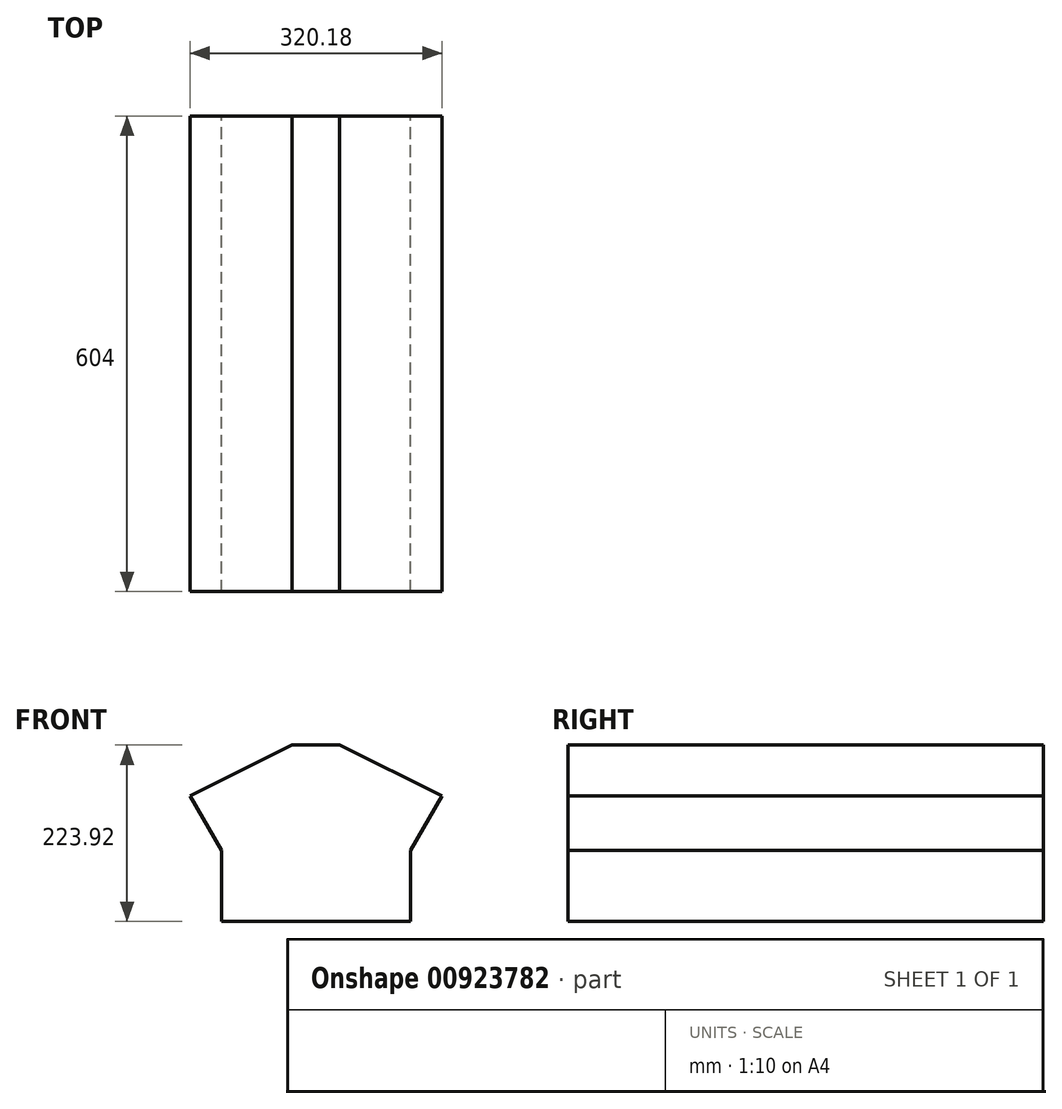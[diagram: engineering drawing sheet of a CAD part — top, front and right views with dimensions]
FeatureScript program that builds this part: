
annotation { "Feature Type Name" : "Feature", "Feature Type Description" : "" }
export const myFeature = defineFeature(function(context is Context, id is Id, definition is map)
    precondition{}
    {
        {
            var Q0;
            Q0=qCreatedBy(makeId("Front.planeOp"),FACE);
            var sketch = newSketch(context, id + "F0", { "sketchPlane" : qUnion([Q0])});
            skLineSegment(sketch, "E0", {"start": v(0, 0) * mm, "end": v(120, 0) * mm});
            skLineSegment(sketch, "E1", {"start": v(120, 0) * mm, "end": v(120, 90) * mm});
            skLineSegment(sketch, "E2", {"start": v(120, 90) * mm, "end": v(160.1, 159.44) * mm});
            skLineSegment(sketch, "E3", {"start": v(160.1, 159.44) * mm, "end": v(30.22, 223.92) * mm});
            skLineSegment(sketch, "E4", {"start": v(30.22, 223.92) * mm, "end": v(0, 223.92) * mm});
            skLineSegment(sketch, "E5", {"start": v(0, 223.92) * mm, "end": v(0, 0) * mm, "construction": true});
            skPoint(sketch, "E6.startSnap0", {"position": v(95.15, 191.68) * mm});
            skLineSegment(sketch, "E7", {"start": v(95.15, 191.68) * mm, "end": v(0, 0) * mm, "construction": true});
            skPoint(sketch, "E8.orphan", {"position": v(95.15, 241.44) * mm});
            skLineSegment(sketch, "E9.MirrorCS", {"start": v(-30.22, 223.92) * mm, "end": v(0, 223.92) * mm});
            skLineSegment(sketch, "E10.MirrorCS", {"start": v(-160.1, 159.44) * mm, "end": v(-30.22, 223.92) * mm});
            skLineSegment(sketch, "E11.MirrorCS", {"start": v(-120, 90) * mm, "end": v(-160.1, 159.44) * mm});
            skLineSegment(sketch, "E12.MirrorCS", {"start": v(0, 0) * mm, "end": v(-120, 0) * mm});
            skLineSegment(sketch, "E13.MirrorCS", {"start": v(-120, 0) * mm, "end": v(-120, 90) * mm});
            skSolve(sketch);
        }
        {
            var Q0;
            Q0=makeQuery(id+"F0.imprint","IMPRINT",FACE,{"disambiguationData":[TD([[makeQuery(id+"F0.imprint","IMPRINT",EDGE,{"derivedFrom":sQuery(id+"F0.wireOp",EDGE,"E0")}),1.0]])]});
            extrude(context, id + "F1", {"entities" : qUnion([Q0]), "depth" : 604 * mm, "offsetDistance" : 25 * mm});
        }
    });
